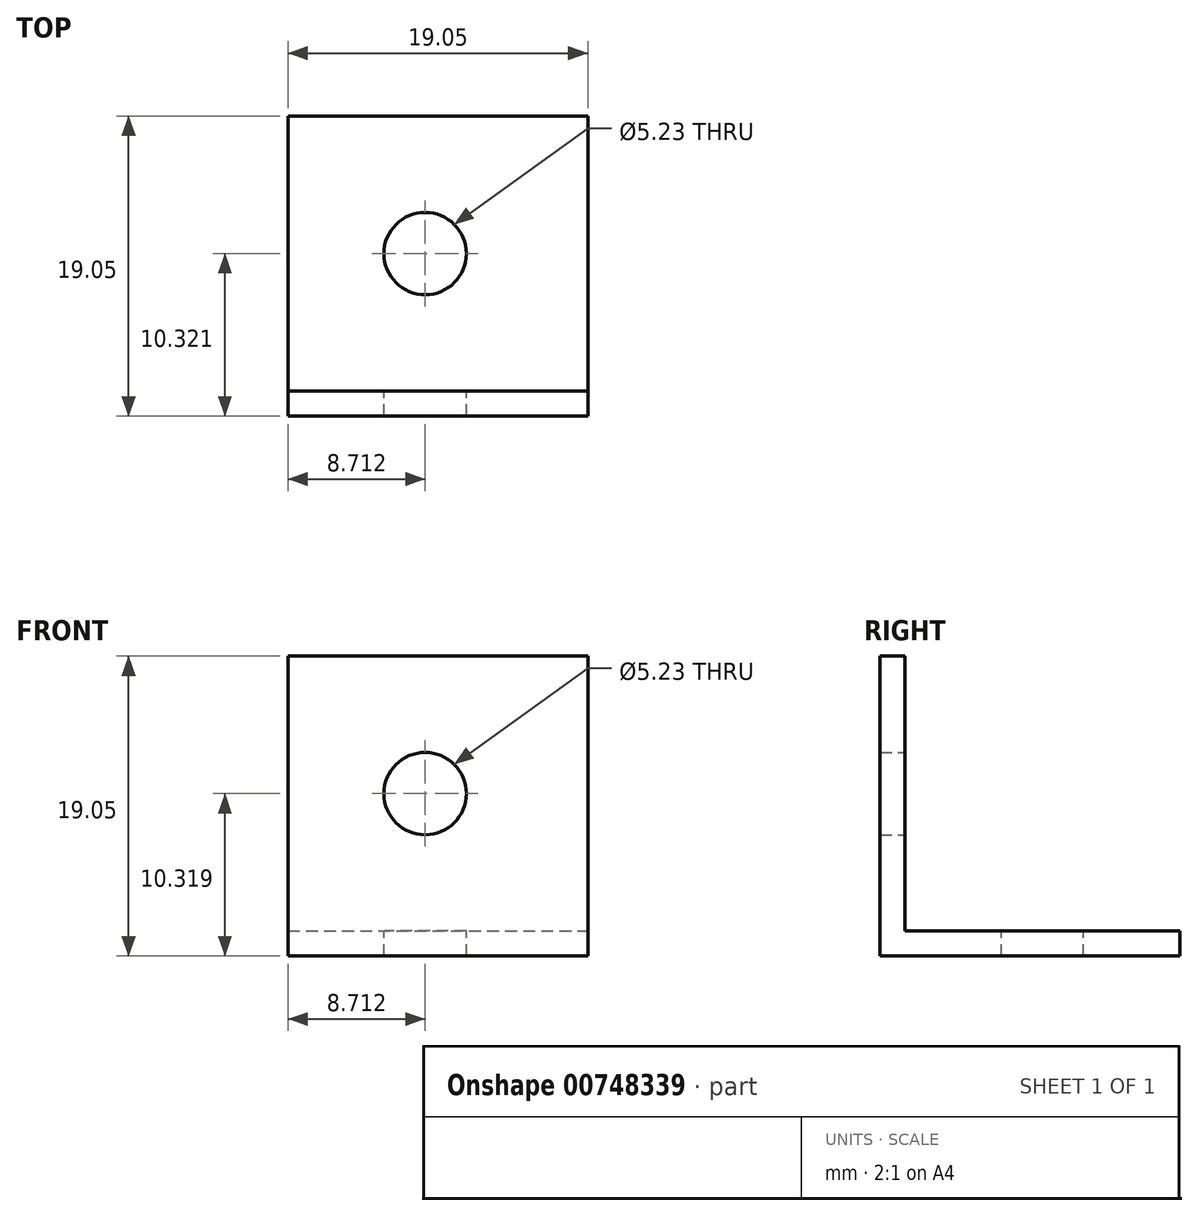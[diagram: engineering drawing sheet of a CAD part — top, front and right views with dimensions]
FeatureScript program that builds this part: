
annotation { "Feature Type Name" : "Feature", "Feature Type Description" : "" }
export const myFeature = defineFeature(function(context is Context, id is Id, definition is map)
    precondition{}
    {
        {
            var Q0;
            Q0=qCreatedBy(makeId("Right.planeOp"),FACE);
            var sketch = newSketch(context, id + "F0", { "sketchPlane" : qUnion([Q0])});
            skLineSegment(sketch, "E0", {"start": v(0, 0) * mm, "end": v(0, -17.46) * mm});
            skLineSegment(sketch, "E1", {"start": v(0, -17.46) * mm, "end": v(17.46, -17.46) * mm});
            skLineSegment(sketch, "E2.0", {"start": v(-1.59, -19.05) * mm, "end": v(17.46, -19.05) * mm});
            skLineSegment(sketch, "E2.1", {"start": v(-1.59, 0) * mm, "end": v(-1.59, -19.05) * mm});
            skLineSegment(sketch, "E3", {"start": v(-1.59, 0) * mm, "end": v(0, 0) * mm});
            skLineSegment(sketch, "E4", {"start": v(17.46, -17.46) * mm, "end": v(17.46, -19.05) * mm});
            skSolve(sketch);
        }
        {
            var Q0;
            Q0=makeQuery(id+"F0.imprint","IMPRINT",FACE,{"disambiguationData":[TD([[makeQuery(id+"F0.imprint","IMPRINT",EDGE,{"derivedFrom":sQuery(id+"F0.wireOp",EDGE,"E0")}),-1.0]])]});
            extrude(context, id + "F1", {"entities" : qUnion([Q0]), "oppositeDirection" : true, "depth" : 19.05 * mm, "offsetDistance" : 25.4 * mm});
        }
        {
            var Q0;
            Q0=makeQuery(id+"F1.opExtrude","SWEPT_FACE",FACE,{"disambiguationData":[OSD([sQuery(id+"F0.wireOp",EDGE,"E1")])]});
            var sketch = newSketch(context, id + "F2", { "sketchPlane" : qUnion([Q0])});
            skLineSegment(sketch, "E5", {"start": v(-19.05, 8.73) * mm, "end": v(0, 8.73) * mm, "construction": true});
            skCircle(sketch, "E6", {"center": v(-10.34, 8.73) * mm, "radius": 2.62 * mm});
            skLineSegment(sketch, "E7", {"start": v(-10.34, 17.46) * mm, "end": v(-10.34, 0) * mm, "construction": true});
            skPoint(sketch, "E7.endSnap0", {"position": v(-9.53, 0) * mm});
            skSolve(sketch);
        }
        {
            var Q0;
            Q0 = qSketchRegion(id + "F2", true);
            extrude(context, id + "F3", {"entities" : qUnion([Q0]), "operationType" : NewBodyOperationType.REMOVE, "oppositeDirection" : true, "depth" : 25.4 * mm, "offsetDistance" : 25.4 * mm});
        }
        {
            var Q0;
            Q0=makeQuery(id+"F1.opExtrude","SWEPT_FACE",FACE,{"disambiguationData":[OSD([sQuery(id+"F0.wireOp",EDGE,"E0")])]});
            var sketch = newSketch(context, id + "F4", { "sketchPlane" : qUnion([Q0])});
            skLineSegment(sketch, "E8", {"start": v(19.05, -8.73) * mm, "end": v(0, -8.73) * mm, "construction": true});
            skCircle(sketch, "E9", {"center": v(10.34, -8.73) * mm, "radius": 2.62 * mm});
            skLineSegment(sketch, "E10", {"start": v(10.34, -17.46) * mm, "end": v(10.34, 0) * mm, "construction": true});
            skSolve(sketch);
        }
        {
            var Q0;
            Q0 = qSketchRegion(id + "F4", true);
            extrude(context, id + "F5", {"entities" : qUnion([Q0]), "operationType" : NewBodyOperationType.REMOVE, "oppositeDirection" : true, "depth" : 25.4 * mm, "offsetDistance" : 25.4 * mm});
        }
    });
